# Revit family: Domotics-DomesticRanges-GEWISS-CHORUS_PLATES_SUPPORT
name_source: partatom
category: Apparecchi elettrici
revit_build: Autodesk Revit 2016 (Build: 20161004_0715(x64)
units: mm (PartAtom-declared; Revit-internal decimal feet)

## family parameters
Basato su piano di lavoro = Sì
Condiviso = No
Mantenere orientamento annotazione = Sì
Punto di calcolo locali = No
Quota connettore circolare = Usa diametro
Sempre verticale = Sì
Taglio con vuoti quando caricato = No
Tipo di parte = Normale

## types (4) — shared parameters
Altezza foro = 45 mm  [stored 0.147638 ft]
Catalogue = DOMOTICS
Catalogue Range = CHORUS - Special plates
Characteristics = Halogen free
Electrocod = 0121
Glow wire test: = 650 °C
IDF = 335af19c-623e-4047-bccf-e3475741a18a
IDT = d13691f8-931b-4039-a4b6-72340c29483b
Immagine tipo = GW16806.jpg
Larghezza foro = 138 mm  [stored 0.452756 ft]
Larghezza supporto = 184 mm  [stored 0.603675 ft]
Materiale supporto = <Per categoria>
Produttore = GEWISS S.p.A.
Prospetto di default = 1219 mm
SEO = Support
Standard; = EN 60669-1
Technical sheet = https://www.gewiss.com
Thermo-pressure with ball = 70
URL = https://www.gewiss.com
Version file RFA = 18.0

## per-type parameters (varying)
| type | Description: | Descrizione | EAN code | Fixing | For box | Modello |
| GW16803 - 3P | 3 gang | SUPPORT, ITALIAN STANDARD, 3-GANG | 8011564274785 | 2 screws (included) | 3 modules | GW16803 |
| GW16806 - 6P | 6 gang | SUPPORT, ITALIAN STANDARD, 6-GANG | 8011564274808 | 4 screws (included) | 6 modules | GW16806 |
| GW16804 - 4P | 4 gang | SUPPORT, ITALIAN STANDARD, 4-GANG | 8011564274792 | 2 screws (included) | 4 modules | GW16804 |
| GW16802 - 2P | 2 gang | SUPPORT, ITALIAN STANDARD, 2-GANG | 8011564274778 | 2 screws (included) | 3 modules | GW16802 |

note: source unit labels omitted for Thermo-pressure with ball — the stored unit's dimension contradicts the parameter name (converter mislabeling)

note: [stored X ft] marks values corroborated as IEEE doubles in the binary element streams (Revit-internal decimal feet)

## geometry (parser evidence)
native form markers: Blend x2
no freeform markers — native parametric forms only
